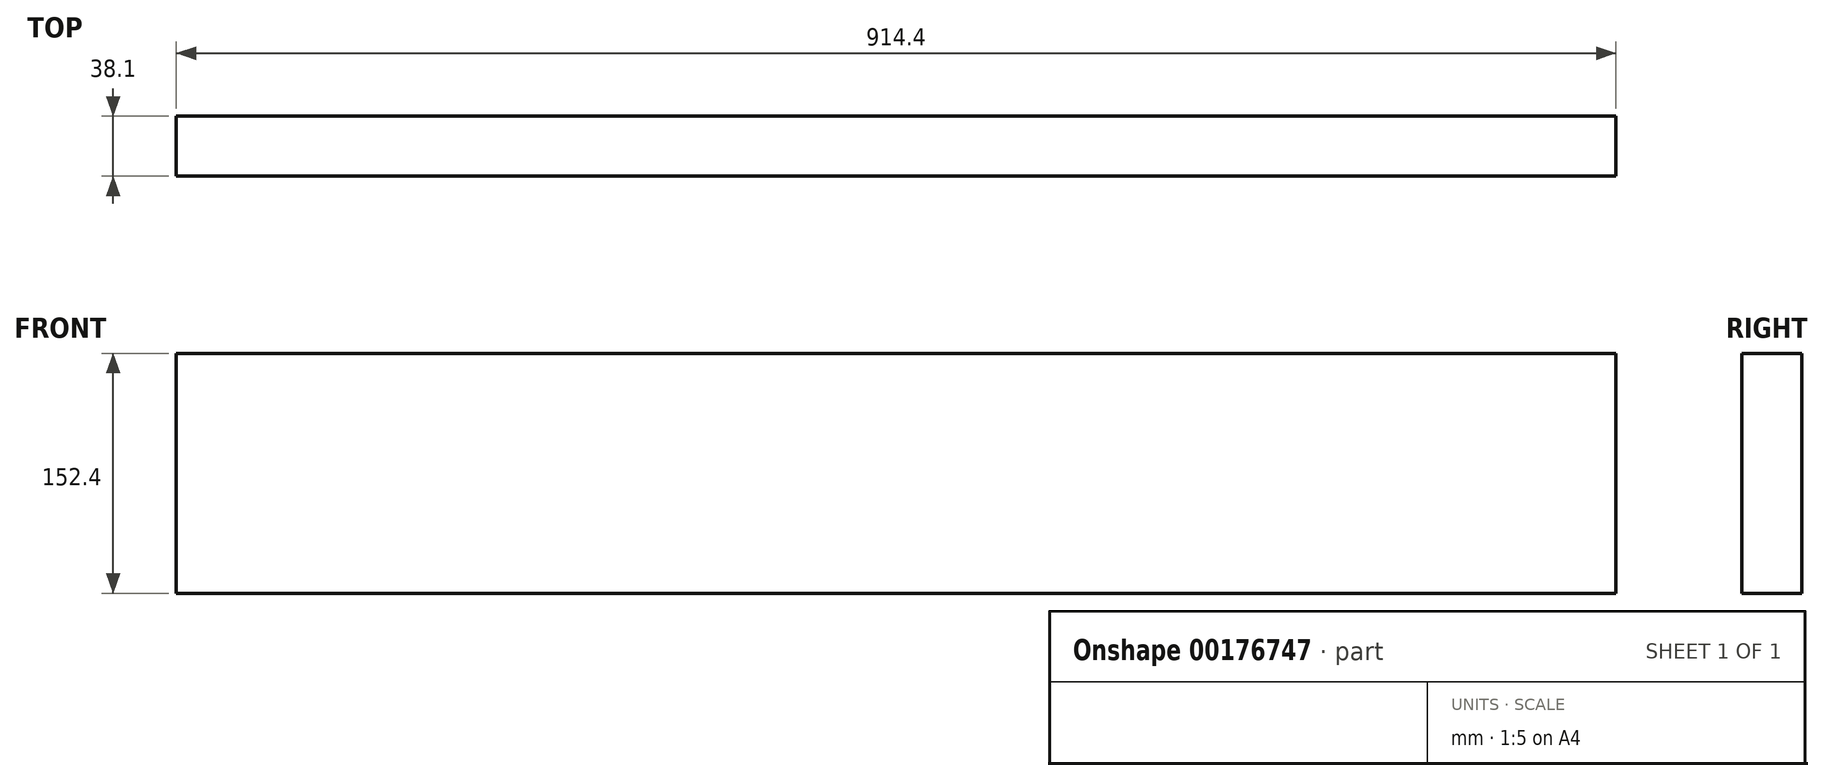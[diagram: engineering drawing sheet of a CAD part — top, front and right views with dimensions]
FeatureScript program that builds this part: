
annotation { "Feature Type Name" : "Feature", "Feature Type Description" : "" }
export const myFeature = defineFeature(function(context is Context, id is Id, definition is map)
    precondition{}
    {
        {
            var Q0;
            Q0=qCreatedBy(makeId("Front.planeOp"),FACE);
            var sketch = newSketch(context, id + "F0", { "sketchPlane" : qUnion([Q0])});
            skLineSegment(sketch, "E0.bottom", {"start": v(0, 0) * mm, "end": v(914.4, 0) * mm});
            skLineSegment(sketch, "E0.top", {"start": v(0, -152.4) * mm, "end": v(914.4, -152.4) * mm});
            skLineSegment(sketch, "E0.left", {"start": v(0, 0) * mm, "end": v(0, -152.4) * mm});
            skLineSegment(sketch, "E0.right", {"start": v(914.4, 0) * mm, "end": v(914.4, -152.4) * mm});
            skSolve(sketch);
        }
        {
            var Q0;
            Q0=makeQuery(id+"F0.imprint","IMPRINT",FACE,{"disambiguationData":[TD([[makeQuery(id+"F0.imprint","IMPRINT",EDGE,{"derivedFrom":sQuery(id+"F0.wireOp",EDGE,"E0.bottom")}),-1.0]])]});
            extrude(context, id + "F1", {"entities" : qUnion([Q0]), "depth" : 38.1 * mm});
        }
    });
